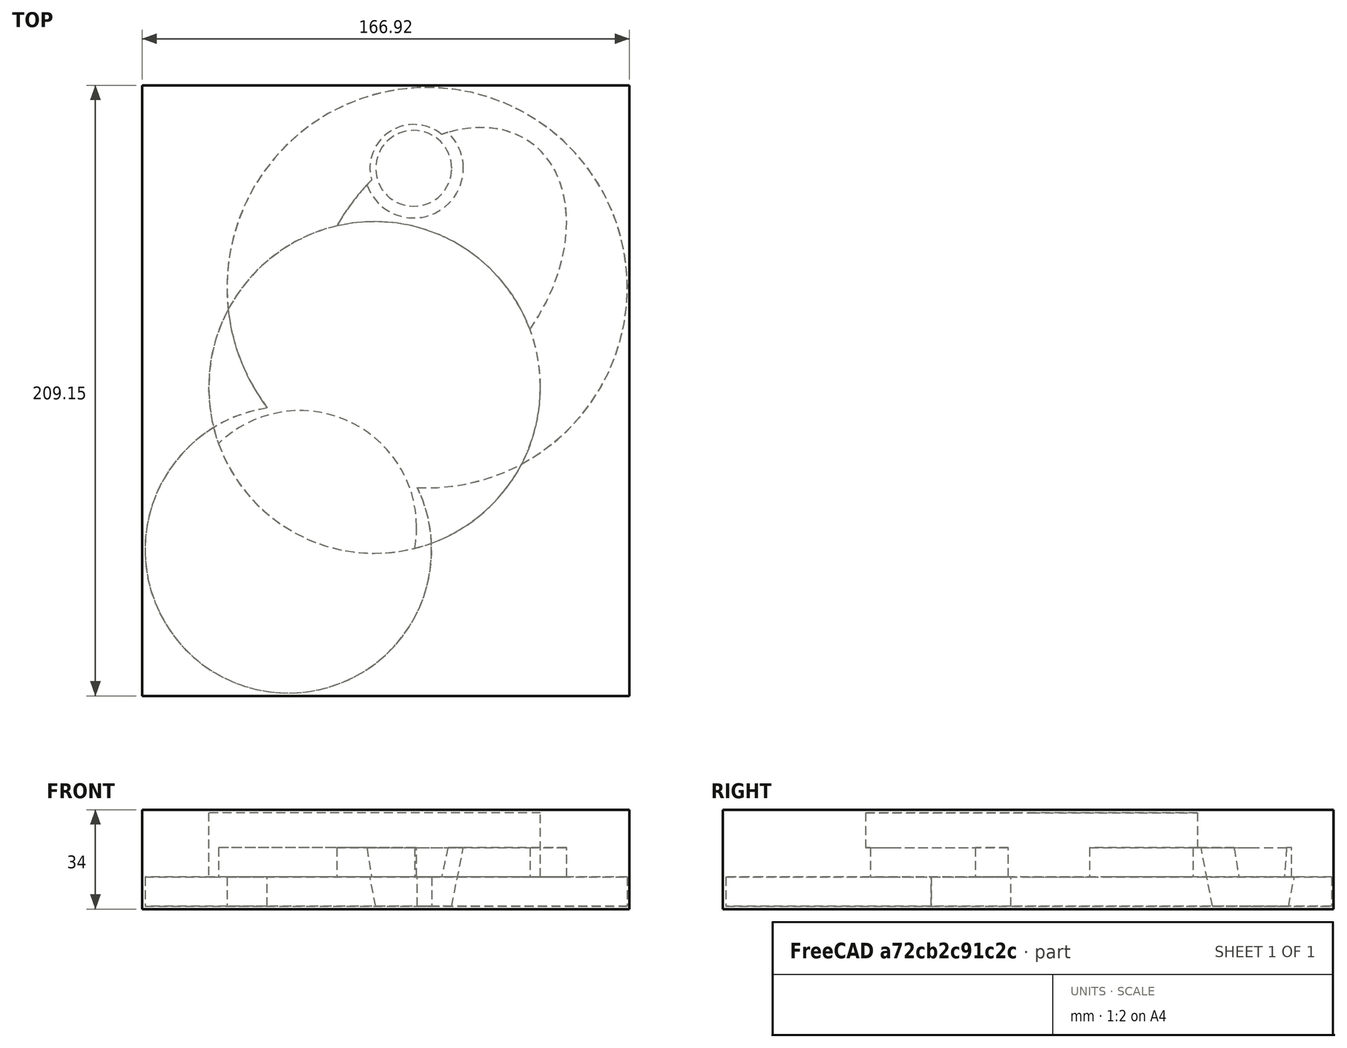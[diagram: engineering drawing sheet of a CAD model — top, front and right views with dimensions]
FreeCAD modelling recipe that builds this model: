
FCSTD DOCUMENT  (FreeCAD 0.19R16653 +9 (Git))
Label: FacePlaning_1
License: CreativeCommons Attribution
LicenseURL: http://creativecommons.org/licenses/by/4.0/
objects: Part::FeaturePython×2, Path::FeaturePython×2, Part::Feature×1, Path::FeatureCompoundPython×1, App::FeaturePython×1, App::DocumentObjectGroup×1
note: 3 computed .brp shape members not serialized (recipe doc carries the construction recipe); baked Part::Feature solids carry a one-line shape summary decoded from their .brp

FEATURE [Part::Feature] planing  label="FacePlaning1"
  shape: bbox 165.2 x 207.4 x 32 mm, 15 faces (baked)
FEATURE [Path::FeatureCompoundPython] Operations  # Path/CAM operation (typed FeaturePython)
  UsePlacements = false
FEATURE [App::FeaturePython] SetupSheet  # Path/CAM operation (typed FeaturePython)
  ClearanceHeightExpression = OpStockZMax+SetupSheet.ClearanceHeightOffset
  ClearanceHeightOffset = 5
  FinalDepthExpression = OpFinalDepth
  HorizRapid = 0
  SafeHeightExpression = OpStockZMax+SetupSheet.SafeHeightOffset
  SafeHeightOffset = 3
  StartDepthExpression = OpStartDepth
  StepDownExpression = OpToolDiameter
  VertRapid = 0
FEATURE [Part::FeaturePython] Clone  label="Model-FacePlaning1"  # Draft clone (typed FeaturePython)
  AttacherType = Attacher::AttachEngine3D
  Fuse = false
  Objects = -> [planing]
  PathResource = Model
  Scale = (1,1,1)
FEATURE [App::DocumentObjectGroup] Model
  Group = -> [Clone]
FEATURE [Path::FeaturePython] Default_Tool  label="Default Tool"  # Path/CAM operation (typed FeaturePython)
  HorizFeed = 0
  HorizRapid = 0
  SpindleDir = 0
  SpindleSpeed = 3000
  ToolNumber = 1
  VertFeed = 0
  VertRapid = 0
  expr: HorizRapid = SetupSheet.HorizRapid
  expr: VertRapid = SetupSheet.VertRapid
FEATURE [Part::FeaturePython] Stock  # WARN: FeaturePython — macro-defined, semantics opaque (R4)
  Base = -> Model
  ExtXneg = 1
  ExtXpos = 1
  ExtYneg = 1
  ExtYpos = 1
  ExtZneg = 1
  ExtZpos = 1
  Placement = pos=(-128.033,-69.7531,0) rot=(0,0,1;0rad)
  StockType = FromBase
FEATURE [Path::FeaturePython] Job  # Path/CAM operation (typed FeaturePython)
  Fixtures = G54
  GeometryTolerance = 0.1
  Model = -> Model
  Operations = -> Operations
  OrderOutputBy = 0
  PostProcessor = 1
  SetupSheet = -> SetupSheet
  SplitOutput = false
  Stock = -> Stock
  ToolController = -> [Default_Tool]
